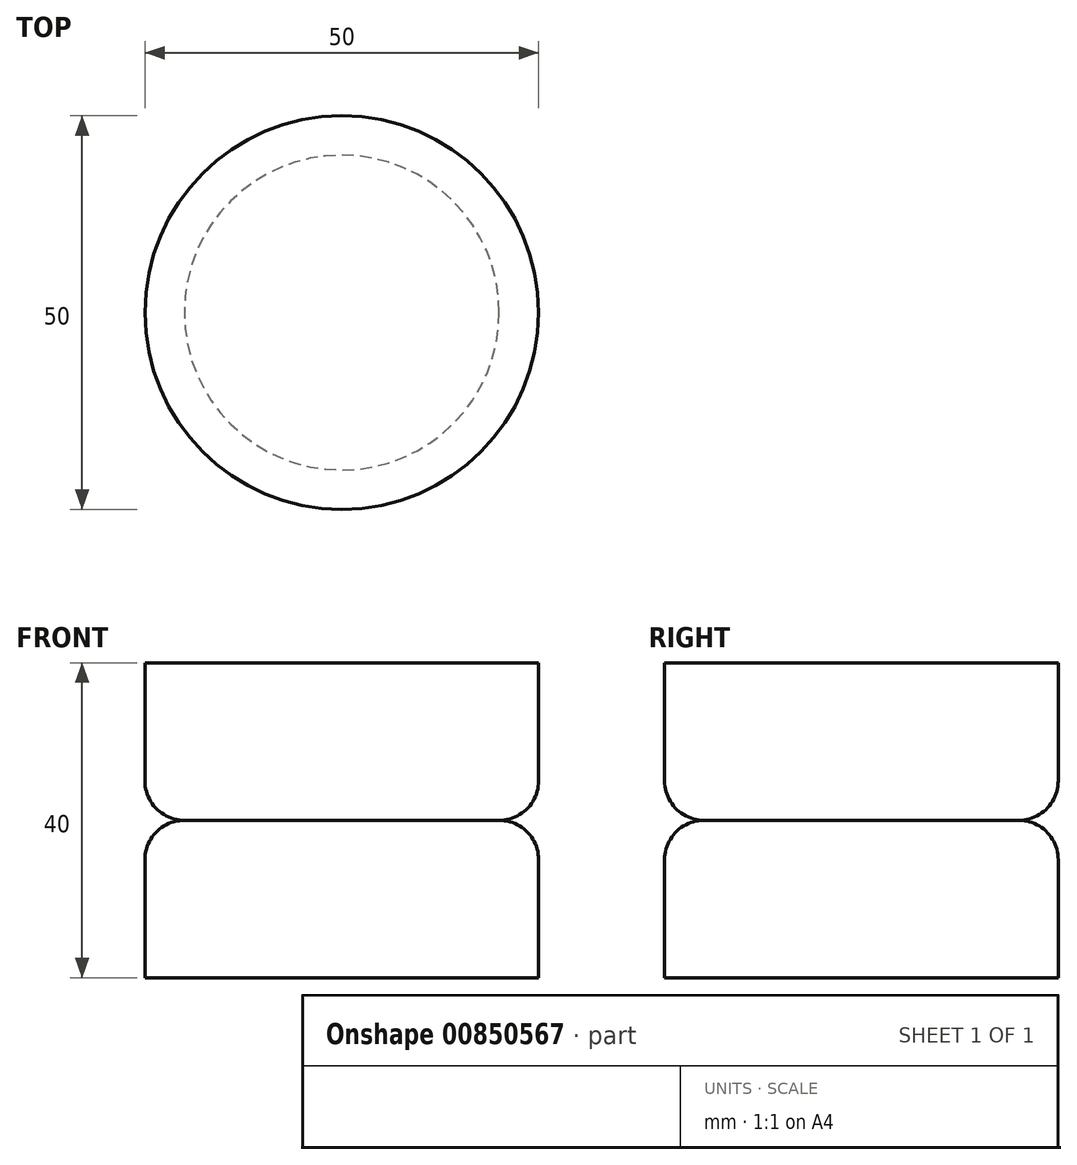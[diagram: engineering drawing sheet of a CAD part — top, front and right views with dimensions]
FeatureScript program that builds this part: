
annotation { "Feature Type Name" : "Feature", "Feature Type Description" : "" }
export const myFeature = defineFeature(function(context is Context, id is Id, definition is map)
    precondition{}
    {
        {
            var Q0;
            Q0=qCreatedBy(makeId("Top.planeOp"),FACE);
            var sketch = newSketch(context, id + "F0", { "sketchPlane" : qUnion([Q0])});
            skCircle(sketch, "E0", {"center": v(0, 0) * mm, "radius": 25 * mm});
            skSolve(sketch);
        }
        {
            var Q0;
            Q0 = qSketchRegion(id + "F0", true);
            extrude(context, id + "F1", {"entities" : qUnion([Q0]), "endBound" : BoundingType.SYMMETRIC, "depth" : 20 * mm, "offsetDistance" : 25.4 * mm});
        }
        {
            var Q0;
            Q0=makeQuery(id+"F1.opExtrude","CAP_EDGE",EDGE,{"disambiguationData":[OSD([sQuery(id+"F0.wireOp",EDGE,"E0")])],"isStart":false});
            fillet(context, id + "F2", {"entities" : qUnion([Q0]), "radius" : 5 * mm, "tangentPropagation" : true, "allowEdgeOverflow" : false});
        }
        {
            var Q0;
            Q0=makeQuery(id+"F1.opExtrude","SWEPT_BODY",BODY,{"disambiguationData":[OSD([sQuery(id+"F0.wireOp",EDGE,"E0")])]});
            var Q1;
            Q1=makeQuery(id+"F1.opExtrude","CAP_FACE",FACE,{"disambiguationData":[OSD([sQuery(id+"F0.wireOp",EDGE,"E0")])],"isStart":false});
            mirror(context, id + "F3", {"operationType" : NewBodyOperationType.ADD, "entities" : qUnion([Q0]), "mirrorPlane" : qUnion([Q1])});
        }
    });
